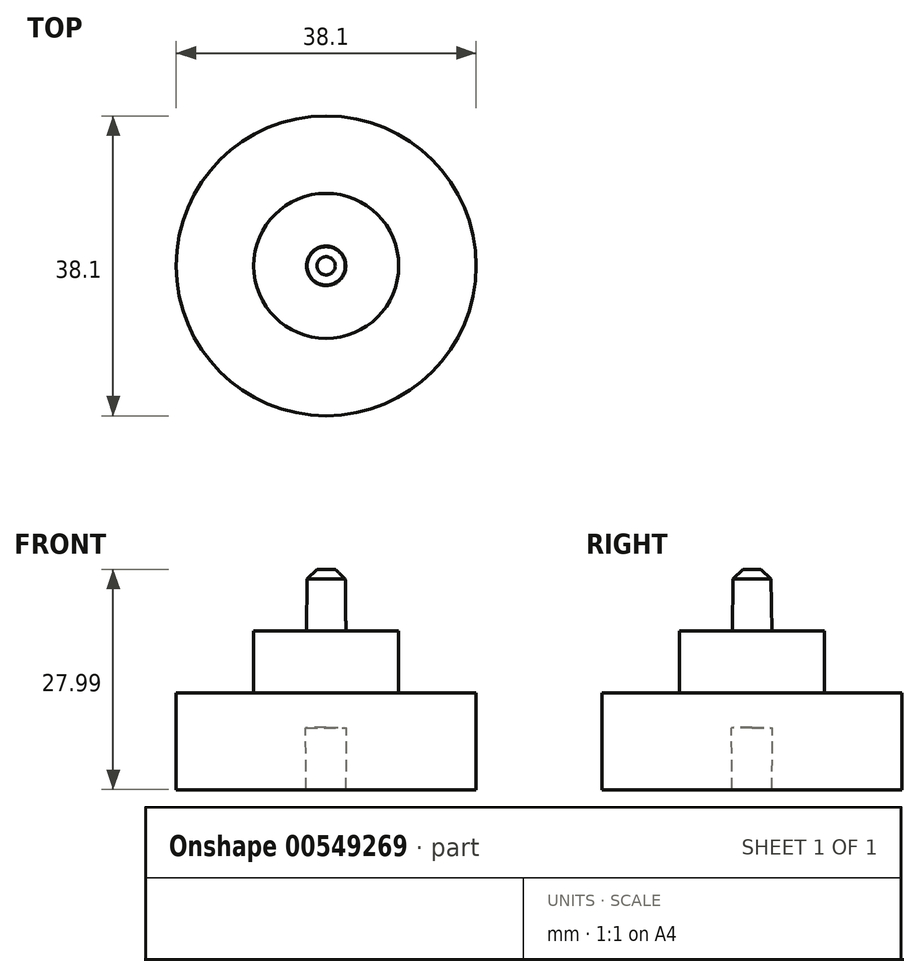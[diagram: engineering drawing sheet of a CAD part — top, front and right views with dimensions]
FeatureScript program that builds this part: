
annotation { "Feature Type Name" : "Feature", "Feature Type Description" : "" }
export const myFeature = defineFeature(function(context is Context, id is Id, definition is map)
    precondition{}
    {
        {
            var Q0;
            Q0=qCreatedBy(makeId("Front.planeOp"),FACE);
            var sketch = newSketch(context, id + "F0", { "sketchPlane" : qUnion([Q0])});
            skLineSegment(sketch, "E0", {"start": v(19.05, 0.43) * mm, "end": v(19.05, 12.7) * mm});
            skPoint(sketch, "E1.orphan", {"position": v(2.41, 13.13) * mm});
            skLineSegment(sketch, "E2", {"start": v(2.54, 0.43) * mm, "end": v(2.6, 8.3) * mm});
            skLineSegment(sketch, "E3", {"start": v(2.6, 8.3) * mm, "end": v(0, 8.32) * mm});
            skLineSegment(sketch, "E4", {"start": v(2.54, 0.43) * mm, "end": v(19.05, 0.43) * mm});
            skLineSegment(sketch, "E5", {"start": v(19.05, 12.7) * mm, "end": v(9.21, 12.7) * mm});
            skLineSegment(sketch, "E6", {"start": v(2.54, 20.57) * mm, "end": v(9.21, 20.57) * mm});
            skLineSegment(sketch, "E7", {"start": v(9.21, 20.57) * mm, "end": v(9.21, 12.7) * mm});
            skPoint(sketch, "E8.end.orphan", {"position": v(0, 12.7) * mm});
            skLineSegment(sketch, "E9", {"start": v(2.54, 20.57) * mm, "end": v(2.5, 20.57) * mm});
            skLineSegment(sketch, "E10", {"start": v(0, 28.42) * mm, "end": v(2.41, 28.42) * mm});
            skLineSegment(sketch, "E11", {"start": v(2.41, 28.42) * mm, "end": v(2.5, 20.57) * mm});
            skPoint(sketch, "E12.orphan", {"position": v(2.54, 17.61) * mm});
            skPoint(sketch, "E13.start.orphan", {"position": v(0, 20.57) * mm});
            skLineSegment(sketch, "E14", {"start": v(0, 28.42) * mm, "end": v(0, 8.32) * mm});
            skSolve(sketch);
        }
        {
            var Q0;
            Q0 = qSketchRegion(id + "F0", true);
            var Q1;
            Q1=sQuery(id+"F0.wireOp",EDGE,"E14");
            revolve(context, id + "F1", {"entities" : qUnion([Q0]), "axis" : qUnion([Q1]), "revolveType" : RevolveType.FULL});
        }
        {
            var Q0;
            Q0=makeQuery(id+"F1.opRevolve","SWEPT_EDGE",EDGE,{"disambiguationData":[OSD([sQuery(id+"F0.wireOp",EDGE,"E10"),sQuery(id+"F0.wireOp",EDGE,"E11")])]});
            chamfer(context, id + "F2", {"entities" : qUnion([Q0]), "width" : 1.27 * mm, "tangentPropagation" : true});
        }
    });
